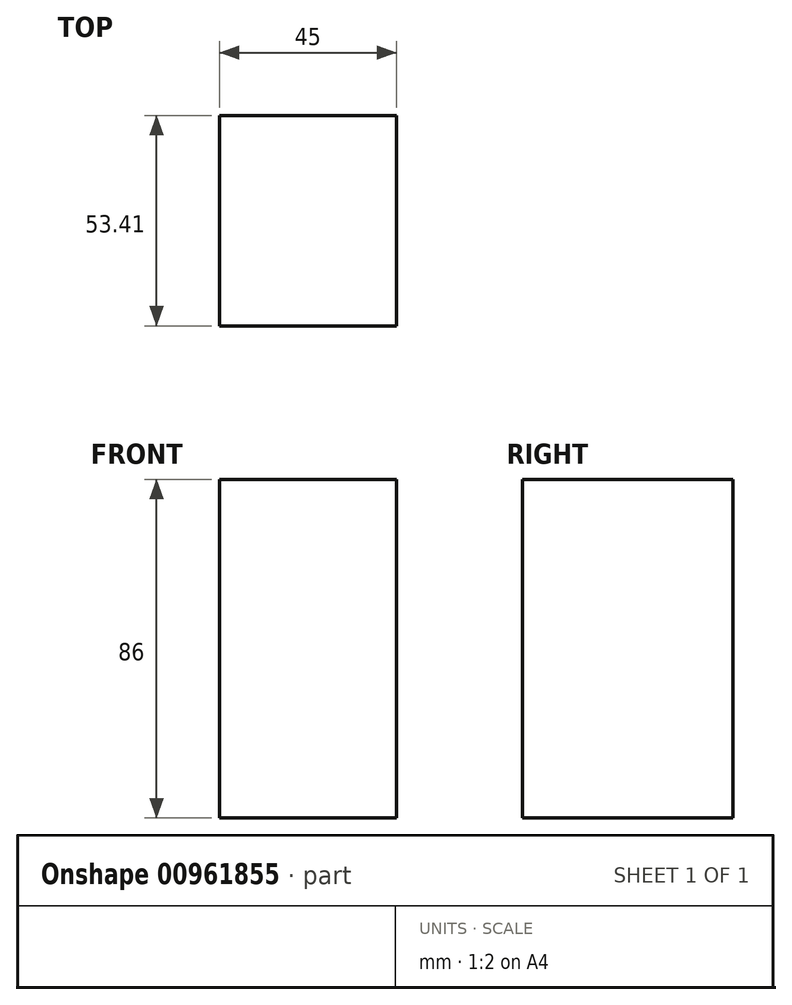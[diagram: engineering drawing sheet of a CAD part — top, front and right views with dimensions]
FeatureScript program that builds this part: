
annotation { "Feature Type Name" : "Feature", "Feature Type Description" : "" }
export const myFeature = defineFeature(function(context is Context, id is Id, definition is map)
    precondition{}
    {
        {
            var Q0;
            Q0=qCreatedBy(makeId("Top.planeOp"),FACE);
            var sketch = newSketch(context, id + "F0", { "sketchPlane" : qUnion([Q0])});
            skLineSegment(sketch, "E0.bottom", {"start": v(-41.3, 51.18) * mm, "end": v(3.7, 51.18) * mm});
            skLineSegment(sketch, "E0.top", {"start": v(-41.3, -2.23) * mm, "end": v(3.7, -2.23) * mm});
            skLineSegment(sketch, "E0.left", {"start": v(-41.3, 51.18) * mm, "end": v(-41.3, -2.23) * mm});
            skLineSegment(sketch, "E0.right", {"start": v(3.7, 51.18) * mm, "end": v(3.7, -2.23) * mm});
            skSolve(sketch);
        }
        {
            var Q0;
            Q0 = qSketchRegion(id + "F0", true);
            extrude(context, id + "F1", {"entities" : qUnion([Q0]), "depth" : 86 * mm, "offsetDistance" : 25 * mm});
        }
    });
